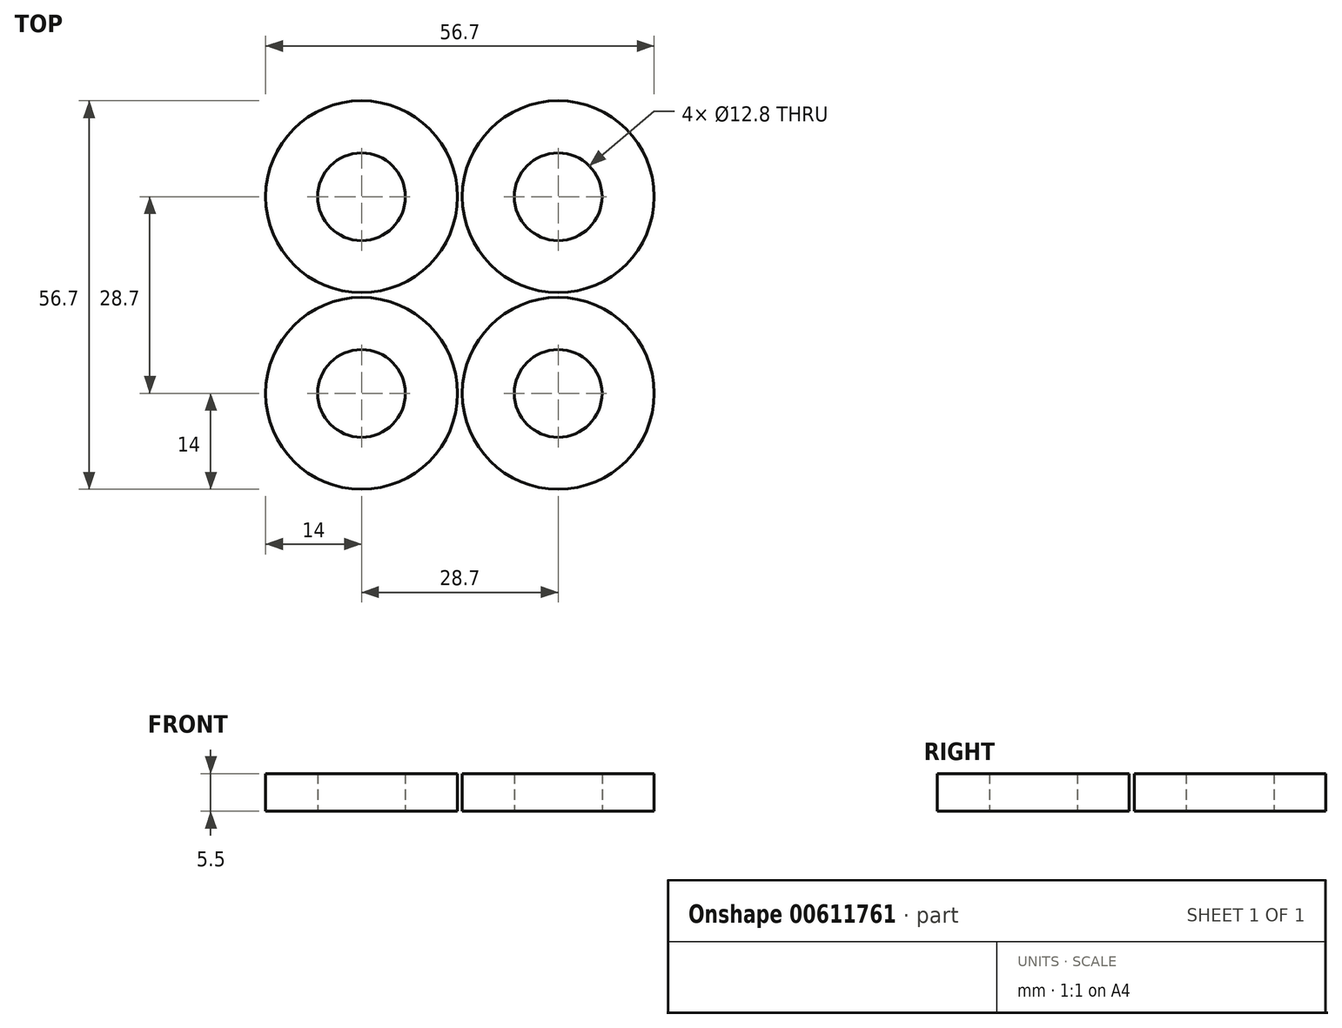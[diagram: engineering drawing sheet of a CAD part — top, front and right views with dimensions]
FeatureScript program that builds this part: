
annotation { "Feature Type Name" : "Feature", "Feature Type Description" : "" }
export const myFeature = defineFeature(function(context is Context, id is Id, definition is map)
    precondition{}
    {
        {
            assignVariable(context, id + "F0", {"name" : "outer", "anyValue" : 28});
        }
        {
            assignVariable(context, id + "F1", {"name" : "depth", "anyValue" : 5.5});
        }
        {
            var Q0;
            Q0=qCreatedBy(makeId("Top.planeOp"),FACE);
            var sketch = newSketch(context, id + "F2", { "sketchPlane" : qUnion([Q0])});
            skCircle(sketch, "E0", {"center": v(0, 0) * mm, "radius": 14 * mm});
            skCircle(sketch, "E1", {"center": v(0, 0) * mm, "radius": 6.4 * mm});
            skSolve(sketch);
        }
        {
            var Q0;
            Q0=makeQuery(id+"F2.imprint","IMPRINT",FACE,{"disambiguationData":[TD([[makeQuery(id+"F2.imprint","IMPRINT",EDGE,{"derivedFrom":sQuery(id+"F2.wireOp",EDGE,"E0")}),1.0]])]});
            extrude(context, id + "F3", {"entities" : qUnion([Q0]), "depth" : (getVariable(context, 'depth')) * mm, "offsetDistance" : 25 * mm});
        }
        {
            var Q0;
            Q0=makeQuery(id+"F3.opExtrude","SWEPT_BODY",BODY,{"disambiguationData":[OSD([sQuery(id+"F2.wireOp",EDGE,"E0"),sQuery(id+"F2.wireOp",EDGE,"E1")])]});
            transform(context, id + "F4", {"entities" : qUnion([Q0]), "transformType" : TransformType.TRANSLATION_3D, "dx" : (getVariable(context, 'outer') + .7) * mm, "dy" : 0 * mm, "dz" : 0 * mm, "makeCopy" : true});
        }
        {
            var Q0;
            Q0=makeQuery(id+"F4.opPattern","COPY",BODY,{"derivedFrom":makeQuery(id+"F3.opExtrude","SWEPT_BODY",BODY,{"disambiguationData":[OSD([sQuery(id+"F2.wireOp",EDGE,"E0"),sQuery(id+"F2.wireOp",EDGE,"E1")])]}),"instanceName":"1"});
            transform(context, id + "F5", {"entities" : qUnion([Q0]), "transformType" : TransformType.TRANSLATION_3D, "dx" : 0 * mm, "dy" : (getVariable(context, 'outer') + .7) * mm, "dz" : 0 * mm, "makeCopy" : true});
        }
        {
            var Q0;
            Q0=makeQuery(id+"F3.opExtrude","SWEPT_BODY",BODY,{"disambiguationData":[OSD([sQuery(id+"F2.wireOp",EDGE,"E0"),sQuery(id+"F2.wireOp",EDGE,"E1")])]});
            transform(context, id + "F6", {"entities" : qUnion([Q0]), "transformType" : TransformType.TRANSLATION_3D, "dx" : 0 * mm, "dy" : (getVariable(context, 'outer') + .7) * mm, "dz" : 0 * mm, "makeCopy" : true});
        }
    });
